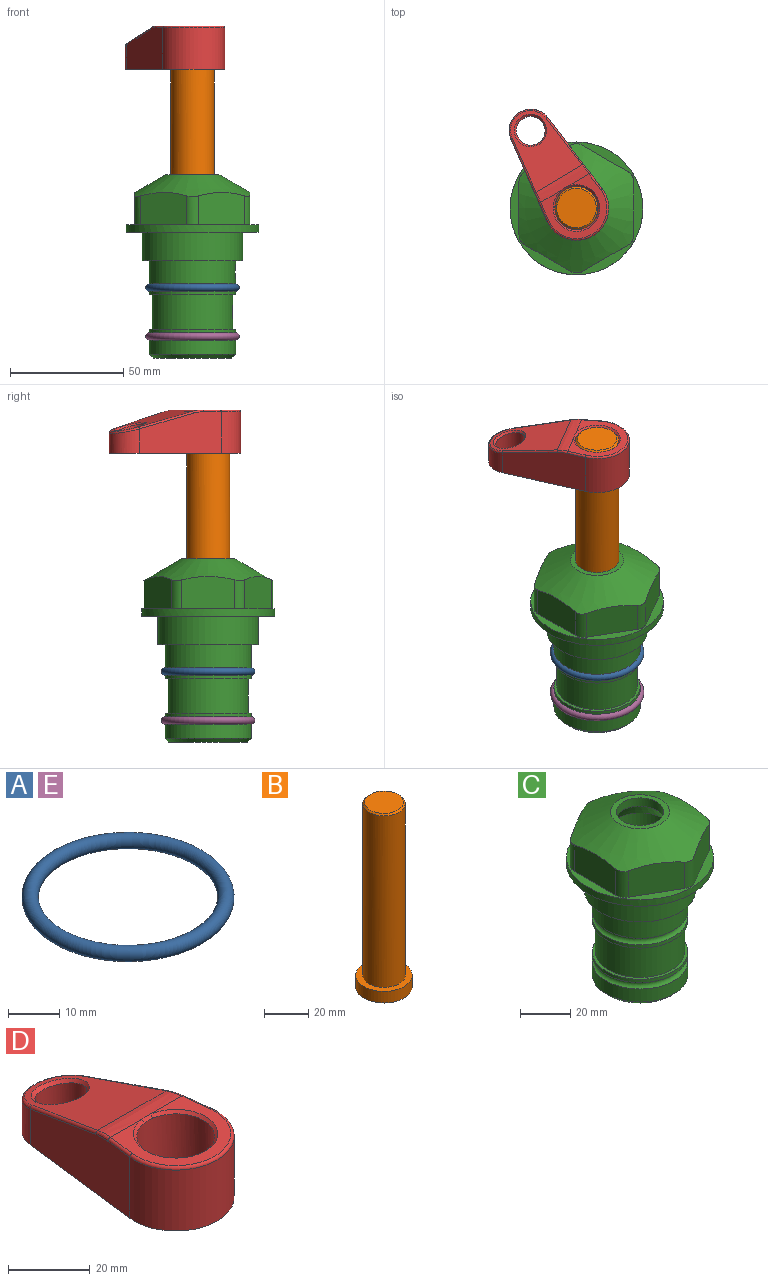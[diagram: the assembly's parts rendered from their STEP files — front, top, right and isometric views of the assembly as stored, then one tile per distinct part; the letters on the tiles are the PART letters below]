
ASSEMBLY  parts=5 mates=4
PART A: 1 faces, bbox 44.7x44.7x3.2 mm
  f0: torus R=19.05mm, axis (0,0,1), area 1193.9mm2
PART B: 6 faces, bbox 25.4x25.4x101.6 mm
  f0: plane 17.46x17.46mm, normal (0,0,1), area 239.5mm2, adj f5
  f1: plane 25.4x25.4mm, normal (0,0,-1), area 506.7mm2, adj f2
  f2: cylinder r=12.7mm len=25.4mm, axis (0,0,1), area 506.7mm2, adj f1,f3
  f3: plane 25.4x25.4mm, normal (0,0,1), area 221.7mm2, adj f2,f4
  f4: cylinder r=9.53mm len=94.46mm, axis (0,0,1), area 5653mm2, adj f3,f5
  f5: cone r=8.73mm half-angle=45deg, axis (0,0,-1), area 64.4mm2, adj f0,f4
PART C: 36 faces, bbox 58.7x58.7x81 mm
  f0: cylinder r=17.78mm len=35.56mm, axis (0,0,1), area 1670.8mm2, adj f23,f24,f31
  f1: cylinder r=19.05mm len=38.1mm, axis (0,0,1), area 1191.9mm2, adj f26,f27,f30
  f2: plane 58.66x58.66mm, normal (0,0,-1), area 1150.6mm2, adj f3,f28
  f3: cylinder r=29.33mm len=58.66mm, axis (0,0,-1), area 585.1mm2, adj f2,f4
  f4: plane 58.66x58.66mm, normal (0,0,1), area 475.9mm2, adj f3,f5,f6,f7,f8,f9,f10,f11
  f5: plane 20.32x14.34mm, normal (-0.5,0.87,0), area 324.4mm2, adj f4,f15,f16,f17
  f6: plane 20.32x14.34mm, normal (0.5,0.87,0), area 324.4mm2, adj f4,f14,f15,f17
  f7: plane 23.48x14.34mm, normal (1,0,0), area 324.4mm2, adj f4,f13,f14,f17
  f8: plane 20.32x14.34mm, normal (0.5,-0.87,0), area 324.4mm2, adj f4,f12,f13,f17
  f9: plane 20.32x14.34mm, normal (-0.5,-0.87,0), area 324.4mm2, adj f4,f11,f12,f17
  f10: plane 23.48x14.34mm, normal (-1,0,0), area 324.4mm2, adj f4,f11,f16,f17
  f11: cylinder r=5.08mm len=12.85mm, axis (0,0,-1), area 67.2mm2, adj f4,f9,f10,f17
  f12: cylinder r=5.08mm len=12.85mm, axis (0,0,-1), area 67.2mm2, adj f4,f8,f9,f17
  f13: cylinder r=5.08mm len=12.85mm, axis (0,0,-1), area 67.2mm2, adj f4,f7,f8,f17
  f14: cylinder r=5.08mm len=12.85mm, axis (0,0,-1), area 67.2mm2, adj f4,f6,f7,f17
  f15: cylinder r=5.08mm len=12.85mm, axis (0,0,-1), area 67.2mm2, adj f4,f5,f6,f17
  f16: cylinder r=5.08mm len=12.85mm, axis (0,0,-1), area 67.2mm2, adj f4,f5,f10,f17
  f17: cone r=11.73mm half-angle=60deg, axis (0,0,-1), area 2071.8mm2, adj f5,f6,f7,f8,f9,f10,f11,f12
  f18: plane 23.46x23.46mm, normal (0,0,1), area 147.4mm2, adj f17,f35
  f19: plane 34.93x34.93mm, normal (0,0,-1), area 958mm2, adj f29
  f20: cylinder r=19.05mm len=38.1mm, axis (0,0,1), area 760.1mm2, adj f21,f29
  f21: torus R=19.05mm, axis (0,0,1), area 565.3mm2, adj f20,f22
  f22: cylinder r=19.05mm len=38.1mm, axis (0,0,1), area 190mm2, adj f21,f23
  f23: plane 38.1x38.1mm, normal (0,0,1), area 146.9mm2, adj f0,f22
  f24: plane 38.1x38.1mm, normal (0,0,-1), area 146.9mm2, adj f0,f25
  f25: cylinder r=19.05mm len=38.1mm, axis (0,0,1), area 190mm2, adj f24,f26
  f26: torus R=19.05mm, axis (0,0,1), area 565.3mm2, adj f1,f25
  f27: plane 44.45x44.45mm, normal (0,0,-1), area 411.7mm2, adj f1,f28
  f28: cylinder r=22.23mm len=44.45mm, axis (0,0,1), area 1773.5mm2, adj f2,f27
  f29: cone r=19.05mm half-angle=45deg, axis (0,0,1), area 257.5mm2, adj f19,f20
  f30: cylinder r=3.17mm len=6.75mm, axis (-1,0,0), area 128mm2, adj f1,f33
  f31: cylinder r=3.17mm len=6.35mm, axis (-1,0,0), area 102.5mm2, adj f0,f33
  f32: plane 25.4x25.4mm, normal (0,0,1), area 506.7mm2, adj f33
  f33: cylinder r=12.7mm len=66.42mm, axis (0,0,-1), area 5236.2mm2, adj f30,f31,f32,f34
  f34: cone r=9.53mm half-angle=30deg, axis (0,0,-1), area 443.4mm2, adj f33,f35
  f35: cylinder r=9.53mm len=19.05mm, axis (0,0,-1), area 240.9mm2, adj f18,f34
PART D: 31 faces, bbox 31.7x65.5x19.8 mm
  f0: plane 39.12x18.26mm, normal (0.99,0.12,0), area 612.2mm2, adj f1,f4,f7,f11,f13,f15
  f1: cylinder r=9.53mm len=18.91mm, axis (0,0,-1), area 296.1mm2, adj f0,f2,f7,f17
  f2: plane 39.12x18.26mm, normal (-0.99,0.12,0), area 612.2mm2, adj f1,f4,f7,f12,f14,f16
  f3: cylinder r=6.35mm len=12.7mm, axis (0,0,-1), area 362.4mm2, adj f7,f18
  f4: cylinder r=14.29mm len=28.58mm, axis (0,0,-1), area 882.2mm2, adj f0,f2,f7,f10
  f5: cylinder r=9.53mm len=19.05mm, axis (0,0,-1), area 1092.6mm2, adj f7,f19,f20
  f6: plane 26.99x23.69mm, normal (0,0,1), area 216.2mm2, adj f9,f10,f11,f12,f19
  f7: plane 63.5x28.58mm, normal (0,0,-1), area 661.8mm2, adj f0,f1,f2,f3,f4,f5,f22,f23
  f8: plane 33.52x23.6mm, normal (0,0.26,0.97), area 486mm2, adj f9,f15,f16,f17,f18
  f9: cylinder r=19.05mm len=24.72mm, axis (1,0,0), area 120.4mm2, adj f6,f8,f13,f14,f20
  f10: torus R=13.49mm, axis (0,0,1), area 59mm2, adj f4,f6,f11,f12
  f11: cylinder r=0.79mm len=8.67mm, axis (0.12,-0.99,0), area 10.8mm2, adj f0,f6,f10,f13
  f12: cylinder r=0.79mm len=8.67mm, axis (0.12,0.99,0), area 10.8mm2, adj f2,f6,f10,f14
  f13: bspline ~4.95x1.42mm, area 6.1mm2, adj f0,f9,f11,f15
  f14: bspline ~4.95x1.42mm, area 6.1mm2, adj f2,f9,f12,f16
  f15: cylinder r=0.79mm len=25.95mm, axis (0.12,-0.96,0.26), area 32.9mm2, adj f0,f8,f13,f17
  f16: cylinder r=0.79mm len=25.95mm, axis (0.12,0.96,-0.26), area 32.9mm2, adj f2,f8,f14,f17
  f17: bspline ~18.91x8.38mm, area 30mm2, adj f1,f8,f15,f16
  f18: bspline ~14.29x14.29mm, area 48.3mm2, adj f3,f8
  f19: cone r=9.53mm half-angle=45deg, axis (0,0,1), area 66.5mm2, adj f5,f6,f20
  f20: bspline ~3.22x0.96mm, area 3.5mm2, adj f5,f9,f19
  f21: plane 2.75x2.72mm, normal (0,0,-1), area 2.9mm2, adj f23,f25,f28
  f22: plane 23.05x15.88mm, normal (-0.99,-0.12,0), area 323.6mm2, adj f7,f25,f26,f27,f28,f29
  f23: plane 23.05x15.88mm, normal (0.99,-0.12,0), area 323.6mm2, adj f7,f21,f25,f27,f28,f30
  f24: cylinder r=9.53mm len=10.69mm, axis (0,0,-1), area 114.7mm2, adj f7,f27,f29,f30
  f25: cylinder r=12.7mm len=20.59mm, axis (0,0,-1), area 381.1mm2, adj f7,f21,f22,f23,f26,f28
  f26: plane 2.75x2.72mm, normal (0,0,-1), area 2.9mm2, adj f22,f25,f28
  f27: plane 19.72x18.37mm, normal (0,-0.26,-0.97), area 291.8mm2, adj f22,f23,f24,f28,f29,f30
  f28: cylinder r=15.88mm len=19.92mm, axis (1,0,0), area 54.8mm2, adj f21,f22,f23,f25,f26,f27
  f29: cylinder r=1.59mm len=11mm, axis (0,0,-1), area 34.7mm2, adj f7,f22,f24,f27
  f30: cylinder r=1.59mm len=11mm, axis (0,0,-1), area 34.7mm2, adj f7,f23,f24,f27
PART E: same geometry as A
PLACE A at identity
PLACE B rot(axis=(0,0,1),30.6deg) t=(0,0,27.55)mm
PLACE C at identity fixed
PLACE D rot(axis=(0,0,1),30.6deg) t=(0,0,27.55)mm
PLACE E t=(0,0,-21.59)mm
MATE fastened A.f0 <-> C.f0  axis (0,0,1) through (0,0,-24.51)mm
MATE cylindrical B.f2 <-> C.f0  axis (0,0,-1) through (0,0,-10.55)mm
MATE fastened B.f2 <-> D.f4  axis (0,0,1) through (0,0,91.05)mm
MATE fastened E.f0 <-> C.f0  axis (0,0,1) through (0,0,-46.1)mm
